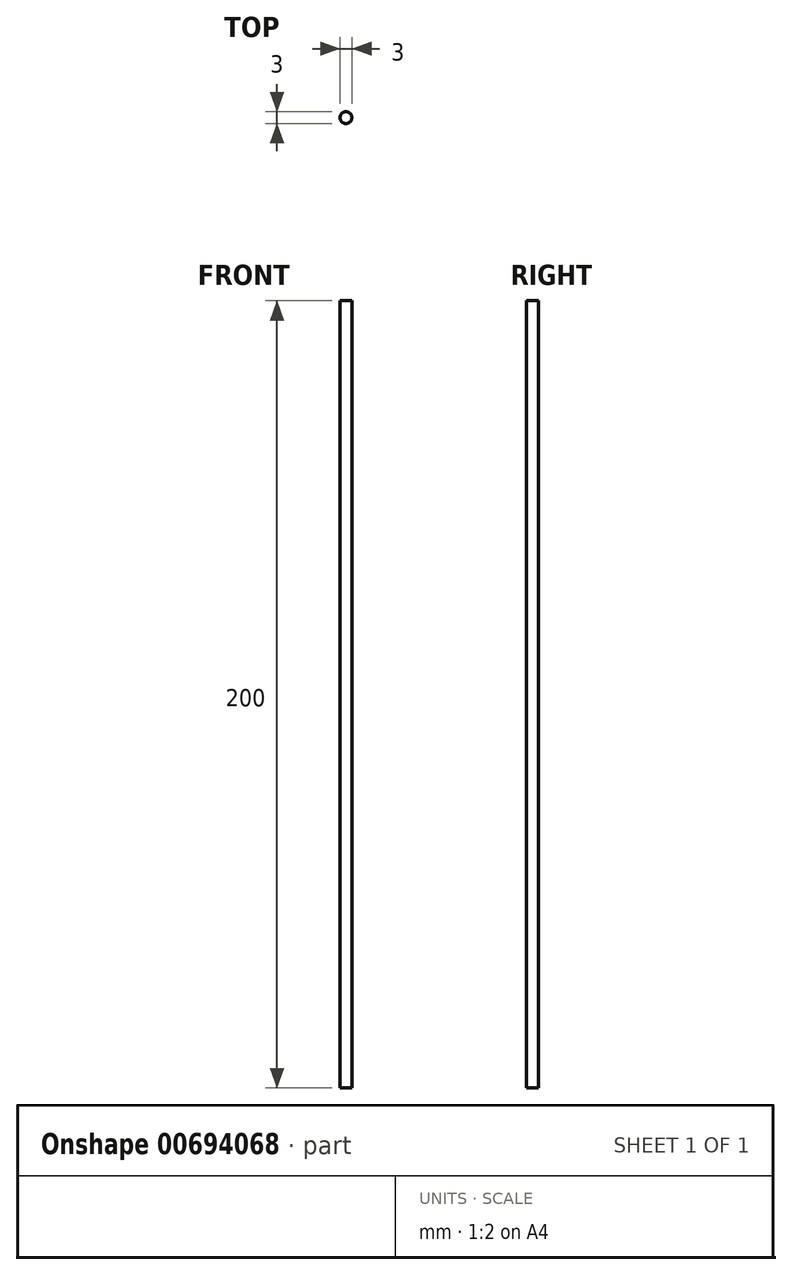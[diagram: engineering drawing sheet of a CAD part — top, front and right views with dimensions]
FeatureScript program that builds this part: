
annotation { "Feature Type Name" : "Feature", "Feature Type Description" : "" }
export const myFeature = defineFeature(function(context is Context, id is Id, definition is map)
    precondition{}
    {
        {
            var Q0;
            Q0=qCreatedBy(makeId("Top.planeOp"),FACE);
            var sketch = newSketch(context, id + "F0", { "sketchPlane" : qUnion([Q0])});
            skCircle(sketch, "E0", {"center": v(-10.67, 12.5) * mm, "radius": 1.5 * mm});
            skSolve(sketch);
        }
        {
            var Q0;
            Q0=makeQuery(id+"F0.imprint","IMPRINT",FACE,{"disambiguationData":[TD([[makeQuery(id+"F0.imprint","IMPRINT",EDGE,{"derivedFrom":sQuery(id+"F0.wireOp",EDGE,"E0")}),1.0]])]});
            extrude(context, id + "F1", {"entities" : qUnion([Q0]), "depth" : 200 * mm, "offsetDistance" : 25 * mm});
        }
    });
